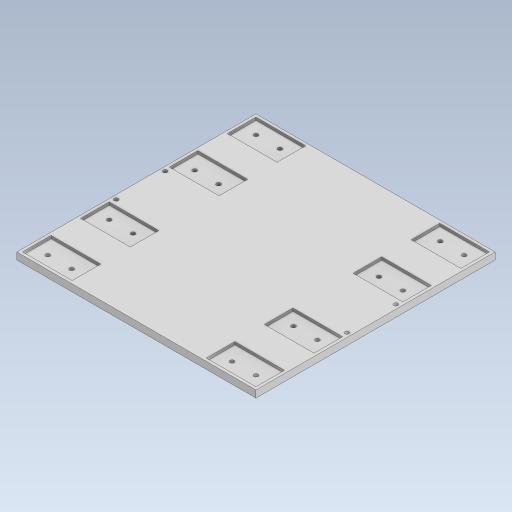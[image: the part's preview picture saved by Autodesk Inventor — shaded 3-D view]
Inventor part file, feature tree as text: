
AUTODESK INVENTOR PART (.ipt)
format: ipt  version: 2023.5 (Build 275446000, 446)  size: 204,288 bytes
history: native  units: in
note: dims shown in document units (in); Inventor stores cm internally (conversion verified against a paired STEP export)
features: extrude x3, sketch x1
ambient origin geometry x8: Origin, YZ Plane, XZ Plane, XY Plane, X Axis, Y Axis, Z Axis, Center Point
bodies: Body1 (feature_tree)
feature tree (4):
  sketch  "Sketch2"  dims[d17=6.6929in d18=6.6929in d19=1.3898in d20=0.7992in d21=0.0787in d22=0.0787in d23=0.7992in d24=0.8268in d25=0.1181in d26=0.3543in d27=0.3543in d28=0.1181in d29=0.6693in d30=0.1181in d31=0.3543in d32=0.3543in d33=0.1181in d34=0.1969in d35=0.0in d36=0.1181in d37=0.0in d38=0.1181in d39=0.1181in d40=0.1575in d41=1.3701in d42=0.1969in d43=0.0in d13=0.0197in d14=0.0344in d15=0.0197in d16=0.0344in d44=0.0197in d45=0.0344in]
  extrude  "Extrusion3"  Depth=6.6929in
  extrude  "Extrusion4"  Depth=1.3898in
  extrude  "Extrusion5"  Depth=0.7992in
